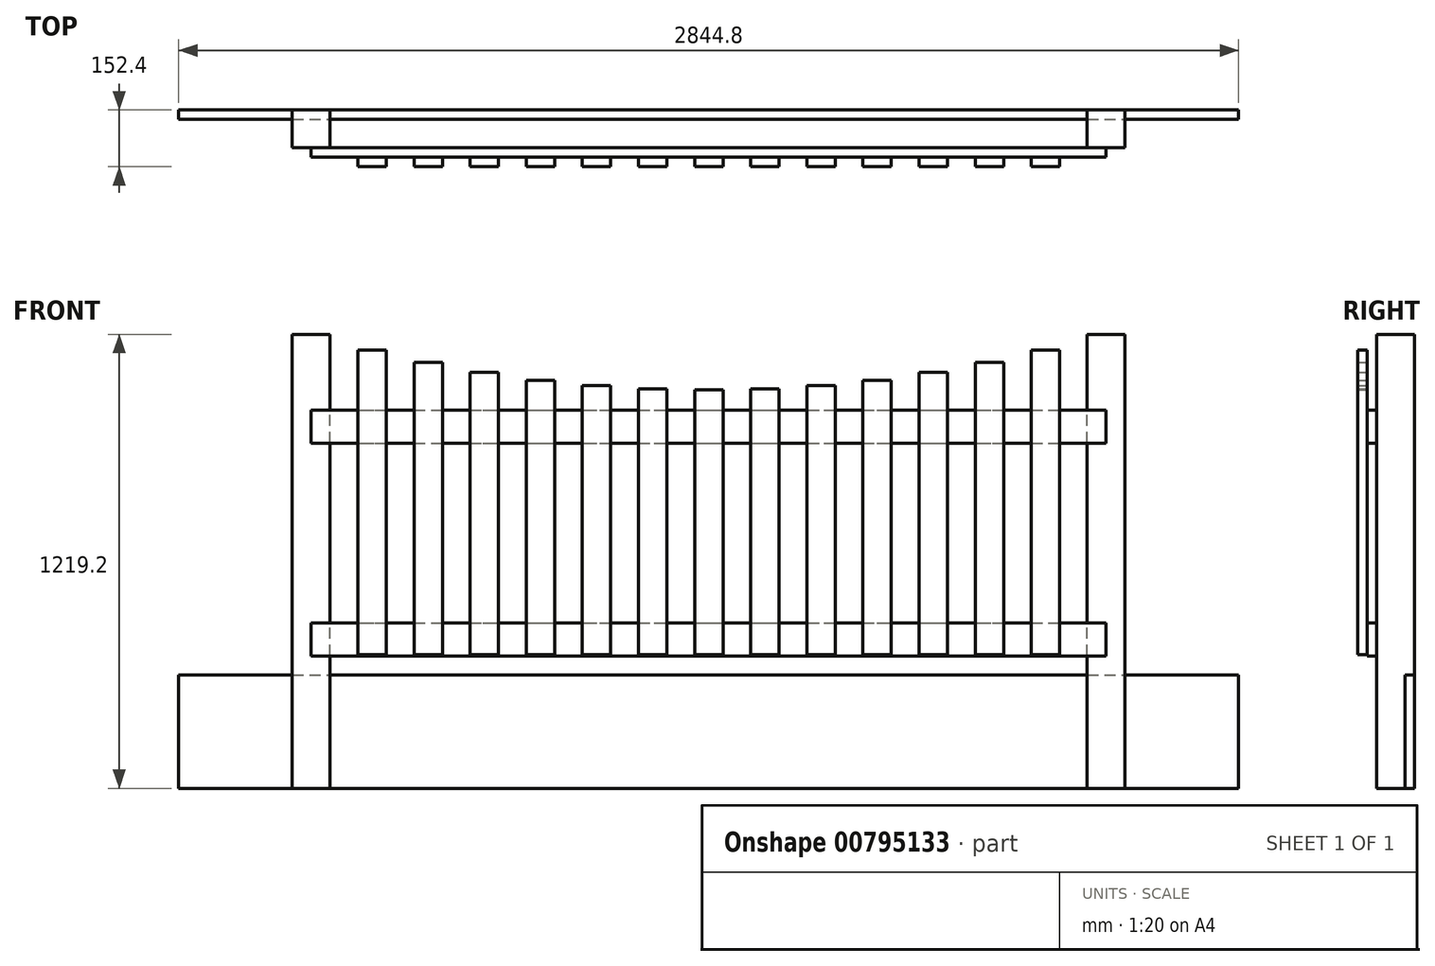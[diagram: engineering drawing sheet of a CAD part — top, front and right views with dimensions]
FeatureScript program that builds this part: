
annotation { "Feature Type Name" : "Feature", "Feature Type Description" : "" }
export const myFeature = defineFeature(function(context is Context, id is Id, definition is map)
    precondition{}
    {
        {
            var Q0;
            Q0=qCreatedBy(makeId("Front.planeOp"),FACE);
            var sketch = newSketch(context, id + "F0", { "sketchPlane" : qUnion([Q0])});
            skLineSegment(sketch, "E0.bottom", {"start": v(-50.8, 0) * mm, "end": v(50.8, 0) * mm});
            skLineSegment(sketch, "E0.top", {"start": v(-50.8, 1371.6) * mm, "end": v(50.8, 1371.6) * mm});
            skLineSegment(sketch, "E0.left", {"start": v(-50.8, 0) * mm, "end": v(-50.8, 1371.6) * mm});
            skLineSegment(sketch, "E0.right", {"start": v(50.8, 0) * mm, "end": v(50.8, 1371.6) * mm});
            skLineSegment(sketch, "E1", {"start": v(0, 0) * mm, "end": v(0, 55) * mm, "construction": true});
            skLineSegment(sketch, "E2.bottom", {"start": v(2082.8, 0) * mm, "end": v(2184.4, 0) * mm});
            skLineSegment(sketch, "E2.top", {"start": v(2082.8, 1371.6) * mm, "end": v(2184.4, 1371.6) * mm});
            skLineSegment(sketch, "E2.left", {"start": v(2082.8, 0) * mm, "end": v(2082.8, 1371.6) * mm});
            skLineSegment(sketch, "E2.right", {"start": v(2184.4, 0) * mm, "end": v(2184.4, 1371.6) * mm});
            skLineSegment(sketch, "E3", {"start": v(2133.6, 0) * mm, "end": v(2133.6, 112.8) * mm, "construction": true});
            skLineSegment(sketch, "E4", {"start": v(-50.8, 457.2) * mm, "end": v(4318, 457.2) * mm, "construction": true});
            skSolve(sketch);
        }
        {
            var Q0;
            Q0 = qSketchRegion(id + "F0", true);
            extrude(context, id + "F1", {"entities" : qUnion([Q0]), "depth" : 101.6 * mm, "offsetDistance" : 25.4 * mm});
        }
        {
            var Q0;
            Q0=qCreatedBy(makeId("Front.planeOp"),FACE);
            var sketch = newSketch(context, id + "F2", { "sketchPlane" : qUnion([Q0])});
            skLineSegment(sketch, "E5.bottom", {"start": v(-355.6, 457.2) * mm, "end": v(2489.2, 457.2) * mm});
            skLineSegment(sketch, "E5.top", {"start": v(-355.6, -50.8) * mm, "end": v(2489.2, -50.8) * mm});
            skLineSegment(sketch, "E5.left", {"start": v(-355.6, 457.2) * mm, "end": v(-355.6, -50.8) * mm});
            skLineSegment(sketch, "E5.right", {"start": v(2489.2, 457.2) * mm, "end": v(2489.2, -50.8) * mm});
            skSolve(sketch);
        }
        {
            var Q0;
            Q0 = qSketchRegion(id + "F2", true);
            extrude(context, id + "F3", {"entities" : qUnion([Q0]), "depth" : 25.4 * mm, "offsetDistance" : 25.4 * mm});
        }
        {
            var Q0;
            Q0=makeQuery(id+"F1.opExtrude","CAP_FACE",FACE,{"disambiguationData":[OSD([sQuery(id+"F0.wireOp",EDGE,"E0.bottom"),sQuery(id+"F0.wireOp",EDGE,"E0.top"),sQuery(id+"F0.wireOp",EDGE,"E0.left"),sQuery(id+"F0.wireOp",EDGE,"E0.right")])],"isStart":false});
            var sketch = newSketch(context, id + "F4", { "sketchPlane" : qUnion([Q0])});
            skLineSegment(sketch, "E6.bottom", {"start": v(0, 596.9) * mm, "end": v(2133.6, 596.9) * mm});
            skLineSegment(sketch, "E6.top", {"start": v(0, 508) * mm, "end": v(2133.6, 508) * mm});
            skLineSegment(sketch, "E6.left", {"start": v(0, 596.9) * mm, "end": v(0, 508) * mm});
            skLineSegment(sketch, "E6.right", {"start": v(2133.6, 596.9) * mm, "end": v(2133.6, 508) * mm});
            skLineSegment(sketch, "E7.bottom", {"start": v(0, 1168.4) * mm, "end": v(2133.6, 1168.4) * mm});
            skLineSegment(sketch, "E7.top", {"start": v(0, 1079.5) * mm, "end": v(2133.6, 1079.5) * mm});
            skLineSegment(sketch, "E7.left", {"start": v(0, 1168.4) * mm, "end": v(0, 1079.5) * mm});
            skLineSegment(sketch, "E7.right", {"start": v(2133.6, 1168.4) * mm, "end": v(2133.6, 1079.5) * mm});
            skSolve(sketch);
        }
        {
            var Q0;
            Q0 = qSketchRegion(id + "F4", true);
            extrude(context, id + "F5", {"entities" : qUnion([Q0]), "depth" : 25.4 * mm, "offsetDistance" : 25.4 * mm});
        }
        {
            var Q0;
            Q0=makeQuery(id+"F5.opExtrude","CAP_FACE",FACE,{"disambiguationData":[OSD([sQuery(id+"F4.wireOp",EDGE,"E6.bottom"),sQuery(id+"F4.wireOp",EDGE,"E6.top"),sQuery(id+"F4.wireOp",EDGE,"E6.left"),sQuery(id+"F4.wireOp",EDGE,"E6.right")])],"isStart":false});
            var sketch = newSketch(context, id + "F6", { "sketchPlane" : qUnion([Q0])});
            skLineSegment(sketch, "E8.bottom", {"start": v(125.22, 511.05) * mm, "end": v(201.42, 511.05) * mm});
            skLineSegment(sketch, "E8.top", {"start": v(125.22, 1328.88) * mm, "end": v(201.42, 1328.88) * mm});
            skLineSegment(sketch, "E8.left", {"start": v(125.22, 511.05) * mm, "end": v(125.22, 1328.88) * mm});
            skLineSegment(sketch, "E8.right", {"start": v(201.42, 511.05) * mm, "end": v(201.42, 1328.88) * mm});
            skLineSegment(sketch, "E9.bottom", {"start": v(275.84, 511.05) * mm, "end": v(352.04, 511.05) * mm});
            skLineSegment(sketch, "E9.top", {"start": v(275.84, 1295.98) * mm, "end": v(352.04, 1295.98) * mm});
            skLineSegment(sketch, "E9.left", {"start": v(275.84, 511.05) * mm, "end": v(275.84, 1295.98) * mm});
            skLineSegment(sketch, "E9.right", {"start": v(352.04, 511.05) * mm, "end": v(352.04, 1295.98) * mm});
            skLineSegment(sketch, "E10.bottom", {"start": v(426.47, 511.05) * mm, "end": v(502.67, 511.05) * mm});
            skLineSegment(sketch, "E10.top", {"start": v(426.47, 1269.28) * mm, "end": v(502.67, 1269.28) * mm});
            skLineSegment(sketch, "E10.left", {"start": v(426.47, 511.05) * mm, "end": v(426.47, 1269.28) * mm});
            skLineSegment(sketch, "E10.right", {"start": v(502.67, 511.05) * mm, "end": v(502.67, 1269.28) * mm});
            skLineSegment(sketch, "E11.bottom", {"start": v(577.09, 511.05) * mm, "end": v(653.29, 511.05) * mm});
            skLineSegment(sketch, "E11.top", {"start": v(577.09, 1248.63) * mm, "end": v(653.29, 1248.63) * mm});
            skLineSegment(sketch, "E11.left", {"start": v(577.09, 511.05) * mm, "end": v(577.09, 1248.63) * mm});
            skLineSegment(sketch, "E11.right", {"start": v(653.29, 511.05) * mm, "end": v(653.29, 1248.63) * mm});
            skLineSegment(sketch, "E12.bottom", {"start": v(727.7, 511.05) * mm, "end": v(803.91, 511.05) * mm});
            skLineSegment(sketch, "E12.top", {"start": v(727.7, 1233.95) * mm, "end": v(803.9, 1233.95) * mm});
            skLineSegment(sketch, "E12.left", {"start": v(727.7, 511.05) * mm, "end": v(727.7, 1233.95) * mm});
            skLineSegment(sketch, "E12.right", {"start": v(803.91, 511.05) * mm, "end": v(803.9, 1233.95) * mm});
            skLineSegment(sketch, "E13.bottom", {"start": v(878.33, 511.05) * mm, "end": v(954.53, 511.05) * mm});
            skLineSegment(sketch, "E13.top", {"start": v(878.33, 1225.17) * mm, "end": v(954.53, 1225.17) * mm});
            skLineSegment(sketch, "E13.left", {"start": v(878.33, 511.05) * mm, "end": v(878.33, 1225.17) * mm});
            skLineSegment(sketch, "E13.right", {"start": v(954.53, 511.05) * mm, "end": v(954.53, 1225.17) * mm});
            skLineSegment(sketch, "E14.bottom", {"start": v(1028.95, 511.05) * mm, "end": v(1105.15, 511.05) * mm});
            skLineSegment(sketch, "E14.top", {"start": v(1028.95, 1222.25) * mm, "end": v(1105.15, 1222.25) * mm});
            skLineSegment(sketch, "E14.left", {"start": v(1028.95, 511.05) * mm, "end": v(1028.95, 1222.25) * mm});
            skLineSegment(sketch, "E14.right", {"start": v(1105.15, 511.05) * mm, "end": v(1105.15, 1222.25) * mm});
            skLineSegment(sketch, "E15.bottom", {"start": v(1179.58, 511.05) * mm, "end": v(1255.78, 511.05) * mm});
            skLineSegment(sketch, "E15.top", {"start": v(1179.58, 1225.17) * mm, "end": v(1255.78, 1225.17) * mm});
            skLineSegment(sketch, "E15.left", {"start": v(1179.58, 511.05) * mm, "end": v(1179.58, 1225.17) * mm});
            skLineSegment(sketch, "E15.right", {"start": v(1255.78, 511.05) * mm, "end": v(1255.78, 1225.17) * mm});
            skLineSegment(sketch, "E16.bottom", {"start": v(1330.2, 511.05) * mm, "end": v(1406.4, 511.05) * mm});
            skLineSegment(sketch, "E16.top", {"start": v(1330.2, 1233.95) * mm, "end": v(1406.4, 1233.95) * mm});
            skLineSegment(sketch, "E16.left", {"start": v(1330.2, 511.05) * mm, "end": v(1330.2, 1233.95) * mm});
            skLineSegment(sketch, "E16.right", {"start": v(1406.4, 511.05) * mm, "end": v(1406.4, 1233.95) * mm});
            skLineSegment(sketch, "E17.bottom", {"start": v(1480.82, 511.05) * mm, "end": v(1557.02, 511.05) * mm});
            skLineSegment(sketch, "E17.top", {"start": v(1480.82, 1248.63) * mm, "end": v(1557.02, 1248.63) * mm});
            skLineSegment(sketch, "E17.left", {"start": v(1480.82, 511.05) * mm, "end": v(1480.82, 1248.63) * mm});
            skLineSegment(sketch, "E17.right", {"start": v(1557.02, 511.05) * mm, "end": v(1557.02, 1248.63) * mm});
            skLineSegment(sketch, "E18.bottom", {"start": v(1631.44, 511.05) * mm, "end": v(1707.64, 511.05) * mm});
            skLineSegment(sketch, "E18.top", {"start": v(1631.44, 1269.28) * mm, "end": v(1707.64, 1269.28) * mm});
            skLineSegment(sketch, "E18.left", {"start": v(1631.44, 511.05) * mm, "end": v(1631.44, 1269.28) * mm});
            skLineSegment(sketch, "E18.right", {"start": v(1707.64, 511.05) * mm, "end": v(1707.64, 1269.28) * mm});
            skLineSegment(sketch, "E19.bottom", {"start": v(1782.06, 511.05) * mm, "end": v(1858.26, 511.05) * mm});
            skLineSegment(sketch, "E19.top", {"start": v(1782.06, 1295.98) * mm, "end": v(1858.26, 1295.98) * mm});
            skLineSegment(sketch, "E19.left", {"start": v(1782.06, 511.05) * mm, "end": v(1782.06, 1295.98) * mm});
            skLineSegment(sketch, "E19.right", {"start": v(1858.26, 511.05) * mm, "end": v(1858.26, 1295.98) * mm});
            skLineSegment(sketch, "E20.bottom", {"start": v(1932.69, 511.05) * mm, "end": v(2008.89, 511.05) * mm});
            skLineSegment(sketch, "E20.top", {"start": v(1932.69, 1328.88) * mm, "end": v(2008.89, 1328.88) * mm});
            skLineSegment(sketch, "E20.left", {"start": v(1932.69, 511.05) * mm, "end": v(1932.69, 1328.88) * mm});
            skLineSegment(sketch, "E20.right", {"start": v(2008.89, 511.05) * mm, "end": v(2008.89, 1328.88) * mm});
            skPoint(sketch, "E21", {"position": v(0, 1371.6) * mm});
            skPoint(sketch, "E22", {"position": v(2133.6, 1371.6) * mm});
            skPoint(sketch, "E23", {"position": v(1067.05, 1222.25) * mm});
            skCircle(sketch, "E24", {"center": v(1067.05, 5105.1) * mm, "radius": 3882.86 * mm, "construction": true});
            skLineSegment(sketch, "E25", {"start": v(1067.05, 1222.25) * mm, "end": v(1067.05, 5105.1) * mm});
            skPoint(sketch, "E26", {"position": v(163.32, 1328.88) * mm});
            skPoint(sketch, "E27", {"position": v(313.94, 1295.98) * mm});
            skPoint(sketch, "E28", {"position": v(464.57, 1269.28) * mm});
            skPoint(sketch, "E29", {"position": v(615.19, 1248.63) * mm});
            skPoint(sketch, "E30", {"position": v(765.8, 1233.95) * mm});
            skPoint(sketch, "E31", {"position": v(916.43, 1225.17) * mm});
            skPoint(sketch, "E32", {"position": v(1217.68, 1225.17) * mm});
            skPoint(sketch, "E33", {"position": v(1368.3, 1233.95) * mm});
            skPoint(sketch, "E34", {"position": v(1518.92, 1248.63) * mm});
            skPoint(sketch, "E35", {"position": v(1669.54, 1269.28) * mm});
            skPoint(sketch, "E36", {"position": v(1820.16, 1295.98) * mm});
            skPoint(sketch, "E37", {"position": v(1970.79, 1328.88) * mm});
            skSolve(sketch);
        }
        {
            var Q0;
            Q0 = qSketchRegion(id + "F6", true);
            extrude(context, id + "F7", {"entities" : qUnion([Q0]), "depth" : 25.4 * mm, "offsetDistance" : 25.4 * mm});
        }
        {
            var Q0;
            Q0=makeQuery(id+"F1.opExtrude","CAP_FACE",FACE,{"disambiguationData":[OSD([sQuery(id+"F0.wireOp",EDGE,"E0.bottom"),sQuery(id+"F0.wireOp",EDGE,"E0.top"),sQuery(id+"F0.wireOp",EDGE,"E0.left"),sQuery(id+"F0.wireOp",EDGE,"E0.right")])],"isStart":false});
            var sketch = newSketch(context, id + "F8", { "sketchPlane" : qUnion([Q0])});
            skLineSegment(sketch, "E38.bottom", {"start": v(-1254.51, 152.4) * mm, "end": v(3609.91, 152.4) * mm});
            skLineSegment(sketch, "E38.top", {"start": v(-1254.51, -427.24) * mm, "end": v(3609.91, -427.24) * mm});
            skLineSegment(sketch, "E38.left", {"start": v(-1254.51, 152.4) * mm, "end": v(-1254.51, -427.24) * mm});
            skLineSegment(sketch, "E38.right", {"start": v(3609.91, 152.4) * mm, "end": v(3609.91, -427.24) * mm});
            skSolve(sketch);
        }
        {
            var Q0;
            Q0 = qSketchRegion(id + "F8", true);
            extrude(context, id + "F9", {"entities" : qUnion([Q0]), "operationType" : NewBodyOperationType.REMOVE, "endBound" : BoundingType.THROUGH_ALL, "oppositeDirection" : true, "depth" : 25.4 * mm, "offsetDistance" : 25.4 * mm});
        }
    });
